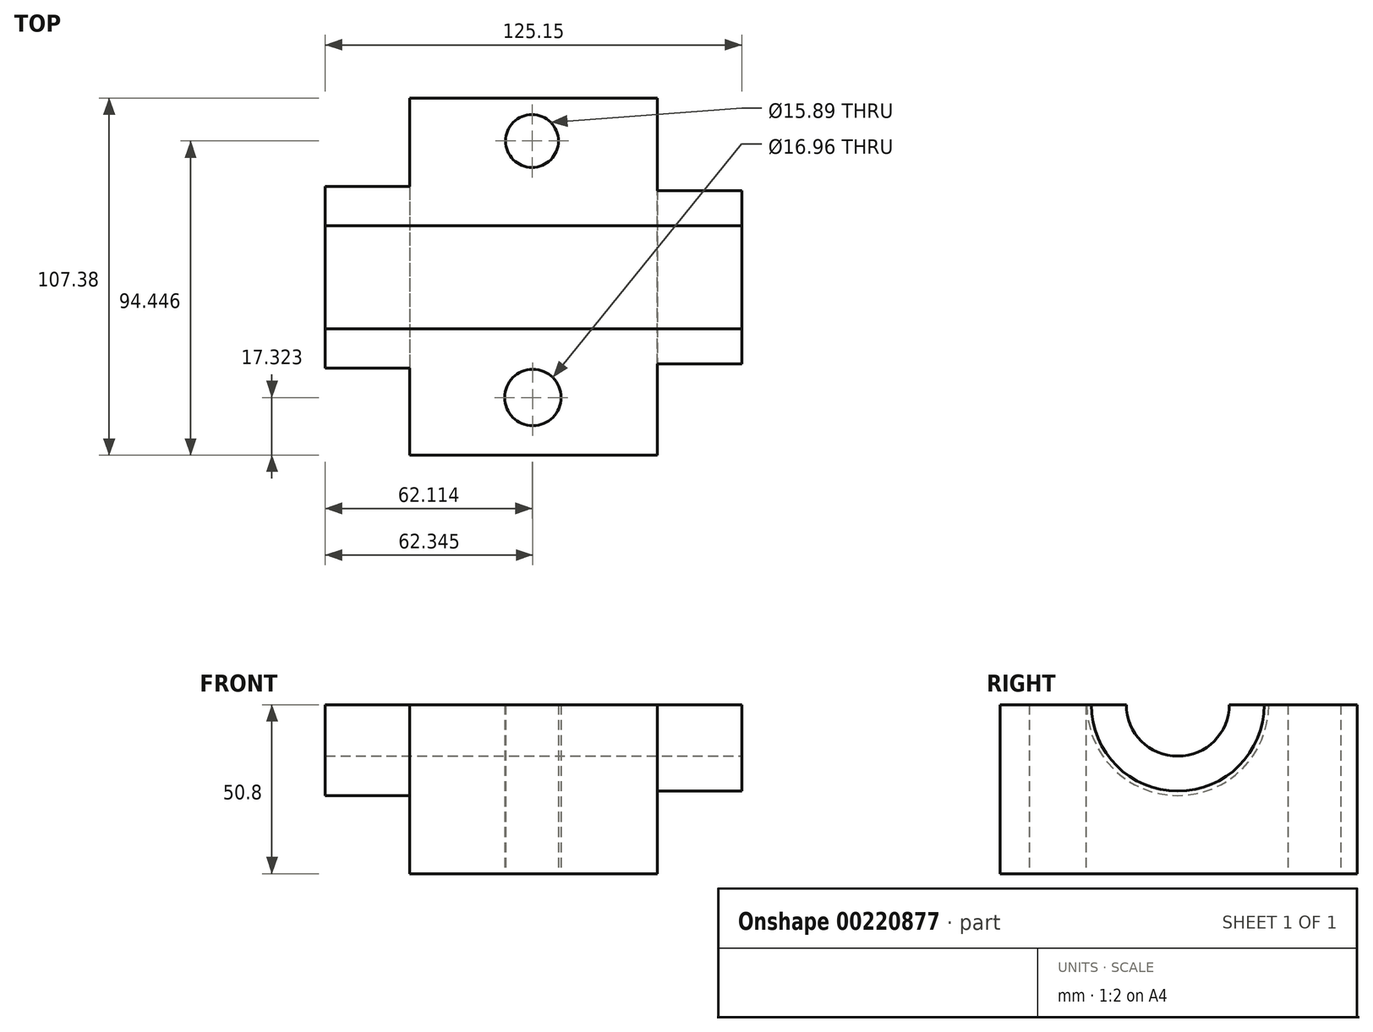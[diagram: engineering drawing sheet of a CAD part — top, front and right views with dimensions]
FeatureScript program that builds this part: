
annotation { "Feature Type Name" : "Feature", "Feature Type Description" : "" }
export const myFeature = defineFeature(function(context is Context, id is Id, definition is map)
    precondition{}
    {
        {
            var Q0;
            Q0=qCreatedBy(makeId("Top.planeOp"),FACE);
            var sketch = newSketch(context, id + "F0", { "sketchPlane" : qUnion([Q0])});
            skLineSegment(sketch, "E0.bottom", {"start": v(30.94, 53.92) * mm, "end": v(-43.41, 53.92) * mm});
            skLineSegment(sketch, "E0.top", {"start": v(30.94, -53.46) * mm, "end": v(-43.41, -53.46) * mm});
            skLineSegment(sketch, "E0.left", {"start": v(30.94, 53.92) * mm, "end": v(30.94, -53.46) * mm});
            skLineSegment(sketch, "E0.right", {"start": v(-43.41, 53.92) * mm, "end": v(-43.41, -53.46) * mm});
            skCircle(sketch, "E1", {"center": v(-6.7, 40.99) * mm, "radius": 7.95 * mm});
            skCircle(sketch, "E2", {"center": v(-6.47, -36.14) * mm, "radius": 8.48 * mm});
            skSolve(sketch);
        }
        {
            var Q0;
            Q0=makeQuery(id+"F0.imprint","IMPRINT",FACE,{"disambiguationData":[TD([[makeQuery(id+"F0.imprint","IMPRINT",EDGE,{"derivedFrom":sQuery(id+"F0.wireOp",EDGE,"E0.bottom")}),1.0]])]});
            extrude(context, id + "F1", {"entities" : qUnion([Q0]), "depth" : 50.8 * mm});
        }
        {
            var Q0;
            Q0=makeQuery(id+"F1.opExtrude","SWEPT_FACE",FACE,{"disambiguationData":[OSD([sQuery(id+"F0.wireOp",EDGE,"E0.right")])]});
            var sketch = newSketch(context, id + "F2", { "sketchPlane" : qUnion([Q0])});
            skCircle(sketch, "E3", {"center": v(0, 50.8) * mm, "radius": 27.34 * mm});
            skCircle(sketch, "E4", {"center": v(0, 50.8) * mm, "radius": 15.47 * mm});
            skSolve(sketch);
        }
        {
            var Q0;
            {var subQ0=sQuery(id+"F2.wireOp",EDGE,"E3");var subQ1=makeQuery(id+"F1.opExtrude","CAP_EDGE",EDGE,{"disambiguationData":[OSD([sQuery(id+"F0.wireOp",EDGE,"E0.right")])],"isStart":false});var subQ2=makeQuery(id+"F2.imprint","INTERSECT",VERTEX,{"disambiguationData":[OD(0.0)],"derivedFrom":[subQ1,subQ0]});Q0=makeQuery(id+"F2.imprint","IMPRINT",FACE,{"disambiguationData":[TD([[makeQuery(id+"F2.imprint","IMPRINT",EDGE,{"disambiguationData":[TD([[subQ2,-1.0]])],"derivedFrom":subQ0}),1.0]])]});}
            extrude(context, id + "F3", {"entities" : qUnion([Q0]), "operationType" : NewBodyOperationType.ADD, "depth" : 25.4 * mm});
        }
        {
            var Q0;
            {var subQ0=sQuery(id+"F0.wireOp",EDGE,"E0.right");var subQ1=sQuery(id+"F2.wireOp",EDGE,"E4");Q0=makeQuery(id+"F3.boolean.opBoolean","SPLIT",FACE,{"disambiguationData":[TD([makeQuery(id+"F3.opExtrude","SWEPT_FACE",FACE,{"disambiguationData":[OSD([subQ1])]})])],"derivedFrom":makeQuery(id+"F1.opExtrude","SWEPT_FACE",FACE,{"disambiguationData":[OSD([subQ0])]})});}
            extrude(context, id + "F4", {"entities" : qUnion([Q0]), "operationType" : NewBodyOperationType.REMOVE, "oppositeDirection" : true, "depth" : 76.2 * mm});
        }
        {
            var Q0;
            Q0=makeQuery(id+"F1.opExtrude","SWEPT_FACE",FACE,{"disambiguationData":[OSD([sQuery(id+"F0.wireOp",EDGE,"E0.left")])]});
            var sketch = newSketch(context, id + "F5", { "sketchPlane" : qUnion([Q0])});
            skCircle(sketch, "E5", {"center": v(0, 50.8) * mm, "radius": 26 * mm});
            skSolve(sketch);
        }
        {
            var Q0;
            {var subQ1=sQuery(id+"F0.wireOp",EDGE,"E0.left");var subQ2=makeQuery(id+"F1.opExtrude","SWEPT_FACE",FACE,{"disambiguationData":[OSD([subQ1])]});var subQ3=sQuery(id+"F2.wireOp",EDGE,"E4");var subQ4=makeQuery(id+"F4.opExtrude","SWEPT_FACE",FACE,{"disambiguationData":[OSD([subQ3])]});var subQ19=makeQuery(id+"F4.boolean.opBoolean","INTERSECT",EDGE,{"derivedFrom":[subQ2,subQ4]});Q0=makeQuery(id+"F5.imprint","IMPRINT",FACE,{"disambiguationData":[TD([[makeQuery(id+"F5.imprint","IMPRINT",EDGE,{"derivedFrom":subQ19}),-1.0]])]});}
            extrude(context, id + "F6", {"entities" : qUnion([Q0]), "operationType" : NewBodyOperationType.ADD, "depth" : 25.4 * mm});
        }
    });
